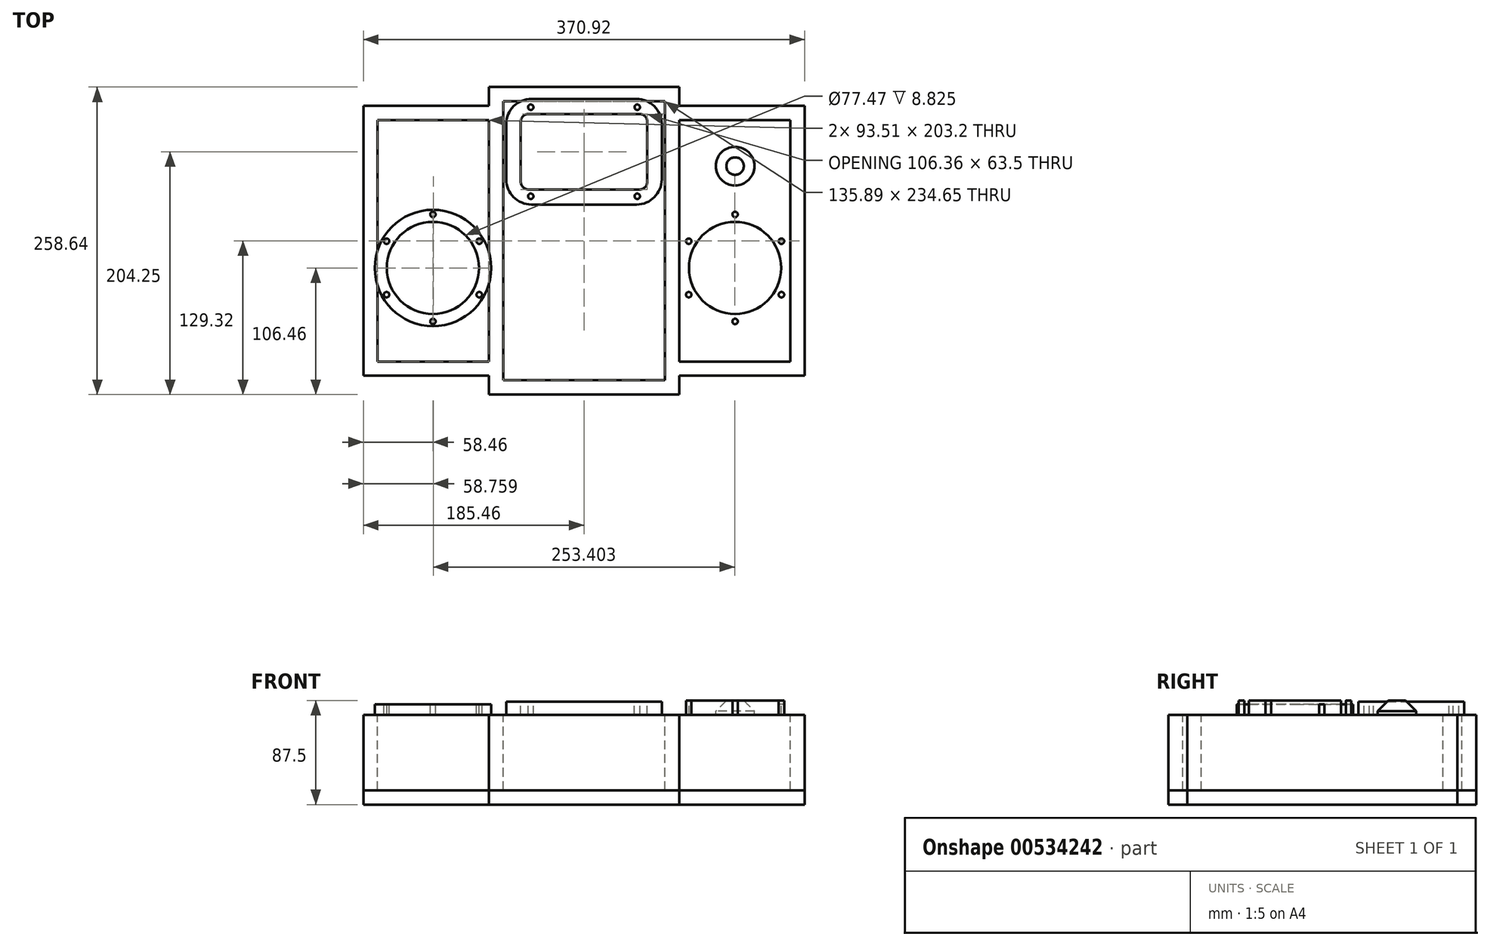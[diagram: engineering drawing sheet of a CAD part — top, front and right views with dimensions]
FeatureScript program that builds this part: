
annotation { "Feature Type Name" : "Feature", "Feature Type Description" : "" }
export const myFeature = defineFeature(function(context is Context, id is Id, definition is map)
    precondition{}
    {
        {
            var Q0;
            Q0=qCreatedBy(makeId("Top.planeOp"),FACE);
            var sketch = newSketch(context, id + "F0", { "sketchPlane" : qUnion([Q0])});
            skLineSegment(sketch, "E0.bottom", {"start": v(-173.62, 132.5) * mm, "end": v(173.62, 132.5) * mm});
            skLineSegment(sketch, "E0.top", {"start": v(-173.62, -132.5) * mm, "end": v(173.62, -132.5) * mm});
            skLineSegment(sketch, "E0.left", {"start": v(-188.63, 117.49) * mm, "end": v(-188.63, -117.49) * mm});
            skLineSegment(sketch, "E0.right", {"start": v(188.63, 117.49) * mm, "end": v(188.63, -117.49) * mm});
            skPoint(sketch, "E0.middle", {"position": v(0, 0) * mm});
            skPoint(sketch, "E1.visualSharp", {"position": v(-188.63, 132.5) * mm});
            skArc(sketch, "E1.filletArc", {"start": v(-173.62, 132.5) * mm, "mid": v(-184.24, 128.1) * mm, "end": v(-188.63, 117.49) * mm});
            skPoint(sketch, "E2.visualSharp", {"position": v(188.63, 132.5) * mm});
            skArc(sketch, "E2.filletArc", {"start": v(188.63, 117.49) * mm, "mid": v(184.24, 128.1) * mm, "end": v(173.62, 132.5) * mm});
            skPoint(sketch, "E3.visualSharp", {"position": v(188.63, -132.5) * mm});
            skArc(sketch, "E3.filletArc", {"start": v(173.62, -132.5) * mm, "mid": v(184.24, -128.1) * mm, "end": v(188.63, -117.49) * mm});
            skPoint(sketch, "E4.visualSharp", {"position": v(-188.63, -132.5) * mm});
            skArc(sketch, "E4.filletArc", {"start": v(-188.63, -117.49) * mm, "mid": v(-184.24, -128.1) * mm, "end": v(-173.62, -132.5) * mm});
            skSolve(sketch);
        }
        {
            var Q0;
            Q0=makeQuery(id+"F0.imprint","IMPRINT",FACE,{"disambiguationData":[TD([[makeQuery(id+"F0.imprint","IMPRINT",EDGE,{"derivedFrom":sQuery(id+"F0.wireOp",EDGE,"E0.bottom")}),-1.0]])]});
            extrude(context, id + "F1", {"entities" : qUnion([Q0]), "oppositeDirection" : true, "depth" : 12 * mm, "offsetDistance" : 25.4 * mm});
        }
        {
            var Q0;
            Q0=makeQuery(id+"F1.opExtrude","CAP_FACE",FACE,{"disambiguationData":[OSD([sQuery(id+"F0.wireOp",EDGE,"E0.bottom"),sQuery(id+"F0.wireOp",EDGE,"E0.top"),sQuery(id+"F0.wireOp",EDGE,"E0.left"),sQuery(id+"F0.wireOp",EDGE,"E0.right"),sQuery(id+"F0.wireOp",EDGE,"E1.filletArc"),sQuery(id+"F0.wireOp",EDGE,"E2.filletArc"),sQuery(id+"F0.wireOp",EDGE,"E3.filletArc"),sQuery(id+"F0.wireOp",EDGE,"E4.filletArc")])],"isStart":true});
            var sketch = newSketch(context, id + "F2", { "sketchPlane" : qUnion([Q0])});
            skLineSegment(sketch, "E5.bottom", {"start": v(46.7, 43.18) * mm, "end": v(-46.7, 43.18) * mm});
            skLineSegment(sketch, "E5.top", {"start": v(46.7, 106.68) * mm, "end": v(-46.7, 106.68) * mm});
            skLineSegment(sketch, "E5.left", {"start": v(53.18, 49.66) * mm, "end": v(53.18, 100.2) * mm});
            skLineSegment(sketch, "E5.right", {"start": v(-53.18, 49.66) * mm, "end": v(-53.18, 100.2) * mm});
            skPoint(sketch, "E5.middle", {"position": v(0, 74.93) * mm});
            skLineSegment(sketch, "E6.bottom", {"start": v(44.2, 30.48) * mm, "end": v(-44.2, 30.48) * mm});
            skLineSegment(sketch, "E6.top", {"start": v(44.2, 119.38) * mm, "end": v(-44.2, 119.38) * mm});
            skLineSegment(sketch, "E6.left", {"start": v(65.34, 51.63) * mm, "end": v(65.34, 98.23) * mm});
            skLineSegment(sketch, "E6.right", {"start": v(-65.34, 51.63) * mm, "end": v(-65.34, 98.23) * mm});
            skPoint(sketch, "E7.visualSharp", {"position": v(-65.34, 119.38) * mm});
            skArc(sketch, "E7.filletArc", {"start": v(-44.2, 119.38) * mm, "mid": v(-59.15, 113.19) * mm, "end": v(-65.34, 98.23) * mm});
            skPoint(sketch, "E8.visualSharp", {"position": v(65.34, 119.38) * mm});
            skArc(sketch, "E8.filletArc", {"start": v(65.34, 98.23) * mm, "mid": v(59.15, 113.19) * mm, "end": v(44.2, 119.38) * mm});
            skPoint(sketch, "E9.visualSharp", {"position": v(65.34, 30.48) * mm});
            skArc(sketch, "E9.filletArc", {"start": v(44.2, 30.48) * mm, "mid": v(59.15, 36.67) * mm, "end": v(65.34, 51.63) * mm});
            skPoint(sketch, "E10.visualSharp", {"position": v(-65.34, 30.48) * mm});
            skArc(sketch, "E10.filletArc", {"start": v(-65.34, 51.63) * mm, "mid": v(-59.15, 36.67) * mm, "end": v(-44.2, 30.48) * mm});
            skPoint(sketch, "E11.visualSharp", {"position": v(53.18, 106.68) * mm});
            skArc(sketch, "E11.filletArc", {"start": v(53.18, 100.2) * mm, "mid": v(51.28, 104.78) * mm, "end": v(46.7, 106.68) * mm});
            skPoint(sketch, "E12.visualSharp", {"position": v(-53.18, 106.68) * mm});
            skArc(sketch, "E12.filletArc", {"start": v(-46.7, 106.68) * mm, "mid": v(-51.28, 104.78) * mm, "end": v(-53.18, 100.2) * mm});
            skPoint(sketch, "E13.visualSharp", {"position": v(-53.18, 43.18) * mm});
            skArc(sketch, "E13.filletArc", {"start": v(-53.18, 49.66) * mm, "mid": v(-51.28, 45.08) * mm, "end": v(-46.7, 43.18) * mm});
            skPoint(sketch, "E14.visualSharp", {"position": v(53.18, 43.18) * mm});
            skArc(sketch, "E14.filletArc", {"start": v(46.7, 43.18) * mm, "mid": v(51.28, 45.08) * mm, "end": v(53.18, 49.66) * mm});
            skCircle(sketch, "E15", {"center": v(0, -50.8) * mm, "radius": 59.7 * mm});
            skCircle(sketch, "E16", {"center": v(0, -50.8) * mm, "radius": 69.22 * mm, "construction": true});
            skLineSegment(sketch, "E17.bottom", {"start": v(56.58, -107.38) * mm, "end": v(-56.58, -107.38) * mm, "construction": true});
            skLineSegment(sketch, "E17.top", {"start": v(56.58, 5.78) * mm, "end": v(-56.58, 5.78) * mm, "construction": true});
            skLineSegment(sketch, "E17.left", {"start": v(56.58, -107.38) * mm, "end": v(56.58, 5.78) * mm, "construction": true});
            skLineSegment(sketch, "E17.right", {"start": v(-56.58, -107.38) * mm, "end": v(-56.58, 5.78) * mm, "construction": true});
            skLineSegment(sketch, "E18", {"start": v(-56.58, 5.78) * mm, "end": v(-17.79, 16.1) * mm, "construction": true});
            skLineSegment(sketch, "E19", {"start": v(56.58, 5.78) * mm, "end": v(17.79, 16.1) * mm, "construction": true});
            skLineSegment(sketch, "E20", {"start": v(56.58, 5.78) * mm, "end": v(66.9, -33.01) * mm, "construction": true});
            skLineSegment(sketch, "E21", {"start": v(56.58, -107.38) * mm, "end": v(66.9, -68.59) * mm, "construction": true});
            skLineSegment(sketch, "E22", {"start": v(56.58, -107.38) * mm, "end": v(17.79, -117.7) * mm, "construction": true});
            skLineSegment(sketch, "E23", {"start": v(-56.58, -107.38) * mm, "end": v(-17.79, -117.7) * mm, "construction": true});
            skLineSegment(sketch, "E24", {"start": v(-56.58, -107.38) * mm, "end": v(-66.9, -68.59) * mm, "construction": true});
            skLineSegment(sketch, "E25", {"start": v(-56.58, 5.78) * mm, "end": v(-66.9, -33.01) * mm, "construction": true});
            skCircle(sketch, "E26", {"center": v(-127, -22.86) * mm, "radius": 48.9 * mm});
            skCircle(sketch, "E27", {"center": v(-127, -22.86) * mm, "radius": 38.73 * mm});
            skCircle(sketch, "E28", {"center": v(-127, 22.14) * mm, "radius": 2.29 * mm});
            skCircle(sketch, "E29.1.0", {"center": v(-88.03, -0.36) * mm, "radius": 2.29 * mm});
            skCircle(sketch, "E29.2.0", {"center": v(-88.03, -45.36) * mm, "radius": 2.29 * mm});
            skCircle(sketch, "E29.3.0", {"center": v(-127, -67.86) * mm, "radius": 2.29 * mm});
            skCircle(sketch, "E29.4.0", {"center": v(-165.97, -45.36) * mm, "radius": 2.29 * mm});
            skCircle(sketch, "E29.5.0", {"center": v(-165.97, -0.36) * mm, "radius": 2.29 * mm});
            skLineSegment(sketch, "E29.anchor1", {"start": v(-127, -22.86) * mm, "end": v(-127, 22.14) * mm, "construction": true});
            skLineSegment(sketch, "E29.anchor2", {"start": v(-127, -22.86) * mm, "end": v(-165.97, -0.36) * mm, "construction": true});
            skCircle(sketch, "E30", {"center": v(-127, 62.87) * mm, "radius": 16.25 * mm});
            skCircle(sketch, "E31.MirrorC", {"center": v(165.97, -0.36) * mm, "radius": 2.29 * mm});
            skCircle(sketch, "E32.MirrorC", {"center": v(127, 22.14) * mm, "radius": 2.29 * mm});
            skCircle(sketch, "E33.MirrorC", {"center": v(88.03, -0.36) * mm, "radius": 2.29 * mm});
            skCircle(sketch, "E34.MirrorC", {"center": v(127, -67.86) * mm, "radius": 2.29 * mm});
            skCircle(sketch, "E35.MirrorC", {"center": v(88.03, -45.36) * mm, "radius": 2.29 * mm});
            skCircle(sketch, "E36.MirrorC", {"center": v(165.97, -45.36) * mm, "radius": 2.29 * mm});
            skLineSegment(sketch, "E37.MirrorCS", {"start": v(127, -22.86) * mm, "end": v(165.97, -0.36) * mm, "construction": true});
            skCircle(sketch, "E38.MirrorC", {"center": v(127, 62.87) * mm, "radius": 16.25 * mm});
            skCircle(sketch, "E39.MirrorC", {"center": v(127, -22.86) * mm, "radius": 48.9 * mm});
            skCircle(sketch, "E40.MirrorC", {"center": v(127, -22.86) * mm, "radius": 38.73 * mm});
            skLineSegment(sketch, "E41.MirrorCS", {"start": v(127, -22.86) * mm, "end": v(127, 22.14) * mm, "construction": true});
            skLineSegment(sketch, "E42", {"start": v(0, 89.81) * mm, "end": v(0, 61.57) * mm, "construction": true});
            skLineSegment(sketch, "E43", {"start": v(-16.64, 74.93) * mm, "end": v(16.75, 74.93) * mm, "construction": true});
            skCircle(sketch, "E44", {"center": v(-44.77, 112.4) * mm, "radius": 2.29 * mm});
            skPoint(sketch, "E44.centerSnap0", {"position": v(-59.15, 113.19) * mm});
            skCircle(sketch, "E45", {"center": v(44.77, 112.4) * mm, "radius": 2.29 * mm});
            skCircle(sketch, "E46", {"center": v(-44.77, 37.46) * mm, "radius": 2.29 * mm});
            skCircle(sketch, "E47", {"center": v(44.77, 37.47) * mm, "radius": 2.29 * mm});
            skCircle(sketch, "E48", {"center": v(-24, 74.93) * mm, "radius": 4.76 * mm, "construction": true});
            skCircle(sketch, "E49", {"center": v(0, 74.93) * mm, "radius": 4.76 * mm, "construction": true});
            skCircle(sketch, "E50", {"center": v(24, 74.93) * mm, "radius": 4.76 * mm, "construction": true});
            skSolve(sketch);
        }
        {
            var Q0;
            Q0=makeQuery(id+"F2.imprint","IMPRINT",FACE,{"disambiguationData":[TD([[makeQuery(id+"F2.imprint","IMPRINT",EDGE,{"derivedFrom":sQuery(id+"F2.wireOp",EDGE,"E30")}),1.0]])]});
            var Q1;
            Q1=makeQuery(id+"F2.imprint","IMPRINT",FACE,{"disambiguationData":[TD([[makeQuery(id+"F2.imprint","IMPRINT",EDGE,{"derivedFrom":sQuery(id+"F2.wireOp",EDGE,"E5.bottom")}),-1.0]])]});
            var Q2;
            Q2=makeQuery(id+"F2.imprint","IMPRINT",FACE,{"disambiguationData":[TD([[makeQuery(id+"F2.imprint","IMPRINT",EDGE,{"derivedFrom":sQuery(id+"F2.wireOp",EDGE,"E38.MirrorC")}),-1.0]])]});
            var Q3;
            Q3=makeQuery(id+"F2.imprint","IMPRINT",FACE,{"disambiguationData":[TD([[makeQuery(id+"F2.imprint","IMPRINT",EDGE,{"derivedFrom":sQuery(id+"F2.wireOp",EDGE,"E15")}),1.0]])]});
            var Q4;
            Q4=makeQuery(id+"F2.imprint","IMPRINT",FACE,{"disambiguationData":[TD([[makeQuery(id+"F2.imprint","IMPRINT",EDGE,{"derivedFrom":sQuery(id+"F2.wireOp",EDGE,"E40.MirrorC")}),-1.0]])]});
            var Q5;
            Q5=makeQuery(id+"F2.imprint","IMPRINT",FACE,{"disambiguationData":[TD([[makeQuery(id+"F2.imprint","IMPRINT",EDGE,{"derivedFrom":sQuery(id+"F2.wireOp",EDGE,"E27")}),1.0]])]});
            var Q6;
            Q6=makeQuery(id+"F2.imprint","IMPRINT",FACE,{"disambiguationData":[TD([[makeQuery(id+"F2.imprint","IMPRINT",EDGE,{"derivedFrom":sQuery(id+"F2.wireOp",EDGE,"E29.5.0")}),1.0]])]});
            var Q7;
            Q7=makeQuery(id+"F2.imprint","IMPRINT",FACE,{"disambiguationData":[TD([[makeQuery(id+"F2.imprint","IMPRINT",EDGE,{"derivedFrom":sQuery(id+"F2.wireOp",EDGE,"E28")}),1.0]])]});
            var Q8;
            Q8=makeQuery(id+"F2.imprint","IMPRINT",FACE,{"disambiguationData":[TD([[makeQuery(id+"F2.imprint","IMPRINT",EDGE,{"derivedFrom":sQuery(id+"F2.wireOp",EDGE,"E29.1.0")}),1.0]])]});
            var Q9;
            Q9=makeQuery(id+"F2.imprint","IMPRINT",FACE,{"disambiguationData":[TD([[makeQuery(id+"F2.imprint","IMPRINT",EDGE,{"derivedFrom":sQuery(id+"F2.wireOp",EDGE,"E29.2.0")}),1.0]])]});
            var Q10;
            Q10=makeQuery(id+"F2.imprint","IMPRINT",FACE,{"disambiguationData":[TD([[makeQuery(id+"F2.imprint","IMPRINT",EDGE,{"derivedFrom":sQuery(id+"F2.wireOp",EDGE,"E29.4.0")}),1.0]])]});
            var Q11;
            Q11=makeQuery(id+"F2.imprint","IMPRINT",FACE,{"disambiguationData":[TD([[makeQuery(id+"F2.imprint","IMPRINT",EDGE,{"derivedFrom":sQuery(id+"F2.wireOp",EDGE,"E29.3.0")}),1.0]])]});
            var Q12;
            Q12=makeQuery(id+"F2.imprint","IMPRINT",FACE,{"disambiguationData":[TD([[makeQuery(id+"F2.imprint","IMPRINT",EDGE,{"derivedFrom":sQuery(id+"F2.wireOp",EDGE,"E32.MirrorC")}),-1.0]])]});
            var Q13;
            Q13=makeQuery(id+"F2.imprint","IMPRINT",FACE,{"disambiguationData":[TD([[makeQuery(id+"F2.imprint","IMPRINT",EDGE,{"derivedFrom":sQuery(id+"F2.wireOp",EDGE,"E31.MirrorC")}),-1.0]])]});
            var Q14;
            Q14=makeQuery(id+"F2.imprint","IMPRINT",FACE,{"disambiguationData":[TD([[makeQuery(id+"F2.imprint","IMPRINT",EDGE,{"derivedFrom":sQuery(id+"F2.wireOp",EDGE,"E33.MirrorC")}),-1.0]])]});
            var Q15;
            Q15=makeQuery(id+"F2.imprint","IMPRINT",FACE,{"disambiguationData":[TD([[makeQuery(id+"F2.imprint","IMPRINT",EDGE,{"derivedFrom":sQuery(id+"F2.wireOp",EDGE,"E35.MirrorC")}),-1.0]])]});
            var Q16;
            Q16=makeQuery(id+"F2.imprint","IMPRINT",FACE,{"disambiguationData":[TD([[makeQuery(id+"F2.imprint","IMPRINT",EDGE,{"derivedFrom":sQuery(id+"F2.wireOp",EDGE,"E34.MirrorC")}),-1.0]])]});
            var Q17;
            Q17=makeQuery(id+"F2.imprint","IMPRINT",FACE,{"disambiguationData":[TD([[makeQuery(id+"F2.imprint","IMPRINT",EDGE,{"derivedFrom":sQuery(id+"F2.wireOp",EDGE,"E36.MirrorC")}),-1.0]])]});
            var Q18;
            Q18=makeQuery(id+"F2.imprint","IMPRINT",FACE,{"disambiguationData":[TD([[makeQuery(id+"F2.imprint","IMPRINT",EDGE,{"derivedFrom":sQuery(id+"F2.wireOp",EDGE,"E44")}),1.0]])]});
            var Q19;
            Q19=makeQuery(id+"F2.imprint","IMPRINT",FACE,{"disambiguationData":[TD([[makeQuery(id+"F2.imprint","IMPRINT",EDGE,{"derivedFrom":sQuery(id+"F2.wireOp",EDGE,"E45")}),1.0]])]});
            var Q20;
            Q20=makeQuery(id+"F2.imprint","IMPRINT",FACE,{"disambiguationData":[TD([[makeQuery(id+"F2.imprint","IMPRINT",EDGE,{"derivedFrom":sQuery(id+"F2.wireOp",EDGE,"E46")}),1.0]])]});
            var Q21;
            Q21=makeQuery(id+"F2.imprint","IMPRINT",FACE,{"disambiguationData":[TD([[makeQuery(id+"F2.imprint","IMPRINT",EDGE,{"derivedFrom":sQuery(id+"F2.wireOp",EDGE,"E47")}),1.0]])]});
            extrude(context, id + "F3", {"entities" : qUnion([Q0, Q1, Q2, Q3, Q4, Q5, Q6, Q7, Q8, Q9, Q10, Q11, Q12, Q13, Q14, Q15, Q16, Q17, Q18, Q19, Q20, Q21]), "operationType" : NewBodyOperationType.REMOVE, "endBound" : BoundingType.THROUGH_ALL, "oppositeDirection" : true, "depth" : 25.4 * mm, "offsetDistance" : 25.4 * mm});
        }
        {
            var Q0;
            Q0=makeQuery(id+"F2.imprint","IMPRINT",FACE,{"disambiguationData":[TD([[makeQuery(id+"F2.imprint","IMPRINT",EDGE,{"derivedFrom":sQuery(id+"F2.wireOp",EDGE,"E26")}),1.0]])]});
            var Q1;
            Q1=makeQuery(id+"F2.imprint","IMPRINT",FACE,{"disambiguationData":[TD([[makeQuery(id+"F2.imprint","IMPRINT",EDGE,{"derivedFrom":sQuery(id+"F2.wireOp",EDGE,"E31.MirrorC")}),1.0]])]});
            extrude(context, id + "F4", {"entities" : qUnion([Q0, Q1]), "operationType" : NewBodyOperationType.REMOVE, "oppositeDirection" : true, "depth" : 3.17 * mm, "offsetDistance" : 25.4 * mm});
        }
        {
            var Q0;
            Q0=makeQuery(id+"F3.boolean.opBoolean","COPY",EDGE,{"derivedFrom":makeQuery(id+"F3.opExtrude","CAP_EDGE",EDGE,{"disambiguationData":[OSD([sQuery(id+"F2.wireOp",EDGE,"E30")])],"isStart":true})});
            var Q1;
            Q1=makeQuery(id+"F3.boolean.opBoolean","COPY",EDGE,{"derivedFrom":makeQuery(id+"F3.opExtrude","CAP_EDGE",EDGE,{"disambiguationData":[OSD([sQuery(id+"F2.wireOp",EDGE,"E38.MirrorC")])],"isStart":true})});
            var Q2;
            Q2=makeQuery(id+"F3.boolean.opBoolean","COPY",EDGE,{"derivedFrom":makeQuery(id+"F3.opExtrude","CAP_EDGE",EDGE,{"disambiguationData":[OSD([sQuery(id+"F2.wireOp",EDGE,"E15")])],"isStart":true})});
            chamfer(context, id + "F5", {"entities" : qUnion([Q0, Q1, Q2]), "width" : 8.9 * mm, "tangentPropagation" : true});
        }
        {
            var Q0;
            Q0=makeQuery(id+"F2.imprint","IMPRINT",FACE,{"disambiguationData":[TD([[makeQuery(id+"F2.imprint","IMPRINT",EDGE,{"derivedFrom":sQuery(id+"F2.wireOp",EDGE,"E5.bottom")}),1.0]])]});
            var Q1;
            Q1=sQuery(id+"F2.wireOp",EDGE,"E7.filletArc");
            extrude(context, id + "F6", {"entities" : qUnion([Q0]), "operationType" : NewBodyOperationType.REMOVE, "surfaceEntities" : qUnion([Q1]), "oppositeDirection" : true, "depth" : 1.02 * mm, "offsetDistance" : 25.4 * mm});
        }
        {
            var Q0;
            Q0=makeQuery(id+"F1.opExtrude","CAP_FACE",FACE,{"disambiguationData":[OSD([sQuery(id+"F0.wireOp",EDGE,"E0.bottom"),sQuery(id+"F0.wireOp",EDGE,"E0.top"),sQuery(id+"F0.wireOp",EDGE,"E0.left"),sQuery(id+"F0.wireOp",EDGE,"E0.right"),sQuery(id+"F0.wireOp",EDGE,"E1.filletArc"),sQuery(id+"F0.wireOp",EDGE,"E2.filletArc"),sQuery(id+"F0.wireOp",EDGE,"E3.filletArc"),sQuery(id+"F0.wireOp",EDGE,"E4.filletArc")])],"isStart":false});
            var sketch = newSketch(context, id + "F7", { "sketchPlane" : qUnion([Q0])});
            skLineSegment(sketch, "E51.bottom", {"start": v(-79.95, 117.32) * mm, "end": v(-67.95, 117.32) * mm});
            skLineSegment(sketch, "E51.top", {"start": v(-79.95, -117.32) * mm, "end": v(-67.95, -117.32) * mm});
            skLineSegment(sketch, "E51.left", {"start": v(-79.95, 117.32) * mm, "end": v(-79.95, -117.32) * mm});
            skLineSegment(sketch, "E51.right", {"start": v(-67.95, 117.32) * mm, "end": v(-67.95, -117.32) * mm});
            skLineSegment(sketch, "E52.bottom", {"start": v(-79.95, 129.32) * mm, "end": v(0, 129.32) * mm});
            skLineSegment(sketch, "E52.top", {"start": v(-79.95, 117.32) * mm, "end": v(0, 117.32) * mm});
            skLineSegment(sketch, "E52.left", {"start": v(-79.95, 129.32) * mm, "end": v(-79.95, 117.32) * mm});
            skLineSegment(sketch, "E52.right", {"start": v(0, 129.32) * mm, "end": v(0, 117.32) * mm});
            skLineSegment(sketch, "E53.bottom", {"start": v(-79.95, -129.32) * mm, "end": v(0, -129.32) * mm});
            skLineSegment(sketch, "E53.top", {"start": v(-79.95, -117.32) * mm, "end": v(0, -117.32) * mm});
            skLineSegment(sketch, "E53.left", {"start": v(-79.95, -129.32) * mm, "end": v(-79.95, -117.32) * mm});
            skLineSegment(sketch, "E53.right", {"start": v(0, -129.32) * mm, "end": v(0, -117.32) * mm});
            skLineSegment(sketch, "E54.bottom", {"start": v(-79.94, 113.6) * mm, "end": v(-185.46, 113.6) * mm});
            skLineSegment(sketch, "E54.top", {"start": v(-79.94, 101.6) * mm, "end": v(-185.46, 101.6) * mm});
            skLineSegment(sketch, "E54.left", {"start": v(-79.94, 113.6) * mm, "end": v(-79.94, 101.6) * mm});
            skLineSegment(sketch, "E54.right", {"start": v(-185.46, 113.6) * mm, "end": v(-185.46, 101.6) * mm});
            skLineSegment(sketch, "E55.bottom", {"start": v(-185.46, 101.6) * mm, "end": v(-173.46, 101.6) * mm});
            skLineSegment(sketch, "E55.top", {"start": v(-185.46, -101.6) * mm, "end": v(-173.46, -101.6) * mm});
            skLineSegment(sketch, "E55.left", {"start": v(-185.46, 101.6) * mm, "end": v(-185.46, -101.6) * mm});
            skLineSegment(sketch, "E55.right", {"start": v(-173.46, 101.6) * mm, "end": v(-173.46, -101.6) * mm});
            skLineSegment(sketch, "E56.bottom", {"start": v(-185.46, -101.6) * mm, "end": v(-79.94, -101.6) * mm});
            skLineSegment(sketch, "E56.top", {"start": v(-185.46, -113.6) * mm, "end": v(-79.95, -113.6) * mm});
            skLineSegment(sketch, "E56.left", {"start": v(-185.46, -101.6) * mm, "end": v(-185.46, -113.6) * mm});
            skLineSegment(sketch, "E56.right", {"start": v(-79.95, -101.6) * mm, "end": v(-79.95, -113.6) * mm});
            skLineSegment(sketch, "E57.MirrorCS", {"start": v(79.95, 117.32) * mm, "end": v(67.95, 117.32) * mm});
            skLineSegment(sketch, "E58.MirrorCS", {"start": v(79.95, 113.6) * mm, "end": v(79.95, 101.6) * mm});
            skLineSegment(sketch, "E59.MirrorCS", {"start": v(79.95, -117.32) * mm, "end": v(67.95, -117.32) * mm});
            skLineSegment(sketch, "E60.MirrorCS", {"start": v(185.46, -101.6) * mm, "end": v(173.46, -101.6) * mm});
            skLineSegment(sketch, "E61.MirrorCS", {"start": v(79.95, -101.6) * mm, "end": v(79.95, -113.6) * mm});
            skLineSegment(sketch, "E62.MirrorCS", {"start": v(185.46, -101.6) * mm, "end": v(185.46, -113.6) * mm});
            skLineSegment(sketch, "E63.MirrorCS", {"start": v(185.46, 113.6) * mm, "end": v(185.46, 101.6) * mm});
            skLineSegment(sketch, "E64.MirrorCS", {"start": v(67.95, 117.32) * mm, "end": v(67.95, -117.32) * mm});
            skLineSegment(sketch, "E65.MirrorCS", {"start": v(185.46, 101.6) * mm, "end": v(185.46, -101.6) * mm});
            skLineSegment(sketch, "E66.MirrorCS", {"start": v(173.46, 101.6) * mm, "end": v(173.46, -101.6) * mm});
            skLineSegment(sketch, "E67.MirrorCS", {"start": v(79.95, 129.32) * mm, "end": v(0, 129.32) * mm});
            skLineSegment(sketch, "E68.MirrorCS", {"start": v(79.95, 117.32) * mm, "end": v(0, 117.32) * mm});
            skLineSegment(sketch, "E69.MirrorCS", {"start": v(79.95, 129.32) * mm, "end": v(79.95, 117.32) * mm});
            skLineSegment(sketch, "E70.MirrorCS", {"start": v(185.46, 101.6) * mm, "end": v(173.46, 101.6) * mm});
            skLineSegment(sketch, "E71.MirrorCS", {"start": v(79.95, -129.32) * mm, "end": v(0, -129.32) * mm});
            skLineSegment(sketch, "E72.MirrorCS", {"start": v(79.95, 117.32) * mm, "end": v(79.95, -117.32) * mm});
            skLineSegment(sketch, "E73.MirrorCS", {"start": v(79.94, 113.6) * mm, "end": v(185.46, 113.6) * mm});
            skLineSegment(sketch, "E74.MirrorCS", {"start": v(185.46, -113.6) * mm, "end": v(79.95, -113.6) * mm});
            skLineSegment(sketch, "E75.MirrorCS", {"start": v(79.94, -129.32) * mm, "end": v(79.94, -117.32) * mm});
            skLineSegment(sketch, "E76.MirrorCS", {"start": v(79.94, 101.6) * mm, "end": v(185.46, 101.6) * mm});
            skLineSegment(sketch, "E77.MirrorCS", {"start": v(185.46, -101.6) * mm, "end": v(79.94, -101.6) * mm});
            skLineSegment(sketch, "E78.MirrorCS", {"start": v(79.95, -117.32) * mm, "end": v(0, -117.32) * mm});
            skSolve(sketch);
        }
        {
            var Q0;
            Q0 = qSketchRegion(id + "F7", true);
            extrude(context, id + "F8", {"entities" : qUnion([Q0]), "depth" : 63.5 * mm, "offsetDistance" : 25.4 * mm});
        }
        {
            var Q0;
            Q0=makeQuery(id+"F8.opExtrude","CAP_FACE",FACE,{"disambiguationData":[OSD([sQuery(id+"F7.wireOp",EDGE,"E51.left"),sQuery(id+"F7.wireOp",EDGE,"E51.right"),sQuery(id+"F7.wireOp",EDGE,"E52.bottom"),sQuery(id+"F7.wireOp",EDGE,"E52.top"),sQuery(id+"F7.wireOp",EDGE,"E52.left"),sQuery(id+"F7.wireOp",EDGE,"E53.bottom"),sQuery(id+"F7.wireOp",EDGE,"E53.top"),sQuery(id+"F7.wireOp",EDGE,"E53.left"),sQuery(id+"F7.wireOp",EDGE,"E54.bottom"),sQuery(id+"F7.wireOp",EDGE,"E54.top"),sQuery(id+"F7.wireOp",EDGE,"E54.right"),sQuery(id+"F7.wireOp",EDGE,"E55.left"),sQuery(id+"F7.wireOp",EDGE,"E55.right"),sQuery(id+"F7.wireOp",EDGE,"E56.bottom"),sQuery(id+"F7.wireOp",EDGE,"E56.top"),sQuery(id+"F7.wireOp",EDGE,"E56.left"),sQuery(id+"F7.wireOp",EDGE,"E62.MirrorCS"),sQuery(id+"F7.wireOp",EDGE,"E63.MirrorCS"),sQuery(id+"F7.wireOp",EDGE,"E64.MirrorCS"),sQuery(id+"F7.wireOp",EDGE,"E65.MirrorCS"),sQuery(id+"F7.wireOp",EDGE,"E66.MirrorCS"),sQuery(id+"F7.wireOp",EDGE,"E67.MirrorCS"),sQuery(id+"F7.wireOp",EDGE,"E68.MirrorCS"),sQuery(id+"F7.wireOp",EDGE,"E69.MirrorCS"),sQuery(id+"F7.wireOp",EDGE,"E71.MirrorCS"),sQuery(id+"F7.wireOp",EDGE,"E72.MirrorCS"),sQuery(id+"F7.wireOp",EDGE,"E73.MirrorCS"),sQuery(id+"F7.wireOp",EDGE,"E74.MirrorCS"),sQuery(id+"F7.wireOp",EDGE,"E75.MirrorCS"),sQuery(id+"F7.wireOp",EDGE,"E76.MirrorCS"),sQuery(id+"F7.wireOp",EDGE,"E77.MirrorCS"),sQuery(id+"F7.wireOp",EDGE,"E78.MirrorCS")])],"isStart":false});
            var sketch = newSketch(context, id + "F9", { "sketchPlane" : qUnion([Q0])});
            skLineSegment(sketch, "E79.0", {"start": v(-185.46, -113.6) * mm, "end": v(-79.95, -113.6) * mm});
            skLineSegment(sketch, "E80.0", {"start": v(-185.46, 113.6) * mm, "end": v(-185.46, -113.6) * mm});
            skLineSegment(sketch, "E81.0", {"start": v(-79.94, 113.6) * mm, "end": v(-185.46, 113.6) * mm});
            skLineSegment(sketch, "E82.0", {"start": v(-79.95, 129.32) * mm, "end": v(-79.95, 113.6) * mm});
            skLineSegment(sketch, "E83.0", {"start": v(-79.95, 129.32) * mm, "end": v(79.95, 129.32) * mm});
            skLineSegment(sketch, "E84.0", {"start": v(79.95, 129.32) * mm, "end": v(79.95, 113.6) * mm});
            skLineSegment(sketch, "E85.0", {"start": v(79.95, 113.6) * mm, "end": v(185.46, 113.6) * mm});
            skLineSegment(sketch, "E86.0", {"start": v(185.46, 113.6) * mm, "end": v(185.46, -113.6) * mm});
            skLineSegment(sketch, "E87.0", {"start": v(185.46, -113.6) * mm, "end": v(79.95, -113.6) * mm});
            skLineSegment(sketch, "E88.0", {"start": v(79.94, -129.32) * mm, "end": v(79.94, -113.6) * mm});
            skLineSegment(sketch, "E89.0", {"start": v(-79.95, -129.32) * mm, "end": v(79.94, -129.32) * mm});
            skLineSegment(sketch, "E90.0", {"start": v(-79.95, -129.32) * mm, "end": v(-79.95, -113.6) * mm});
            skSolve(sketch);
        }
        {
            var Q0;
            Q0 = qSketchRegion(id + "F9", true);
            extrude(context, id + "F10", {"entities" : qUnion([Q0]), "depth" : 12 * mm, "offsetDistance" : 25.4 * mm});
        }
    });
